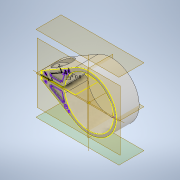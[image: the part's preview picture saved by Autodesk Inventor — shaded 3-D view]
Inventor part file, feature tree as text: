
AUTODESK INVENTOR PART (.ipt)
format: ipt  version: 2022 (Build 260153000, 153)  size: 346,112 bytes
history: native  units: mm
features: other x7, extrude x7, sketch x5, projected_geometry x4, fillet x2, mirror x1
ambient origin geometry x8: Origin, YZ Plane, XZ Plane, XY Plane, X Axis, Y Axis, Z Axis, Center Point
bodies: Body1 (feature_tree)
feature tree (26):
  other  "ソリッド1"
  extrude  "押し出し1"  Depth=31.9mm
  sketch  "スケッチ2"
  sketch  "スケッチ3"
  other  "作業平面1"
  other  "m6hole"
  mirror  "ミラー1"
  other  "HexagonSC"
  extrude  "押し出し2"  Depth=2.0mm
  extrude  "押し出し3"  TaperAngle=120.0deg  [1 undecoded]
  extrude  "押し出し4"  TaperAngle=150.0deg  [1 undecoded]
  sketch  "スケッチ7"
  sketch  "スケッチ8"
  other  "sidescetch"
  extrude  "押し出し5"  Depth=2.0mm
  extrude  "押し出し6"  Depth=2.0mm
  extrude  "押し出し7"  Depth=2.4mm
  fillet  "フィレット1"  Radius=0.8mm
  fillet  "フィレット2"  Radius=0.8mm
  other  "baseScetcj"
  projected_geometry  "投影ループ1"
  projected_geometry  "投影ループ2"
  projected_geometry  "投影ループ3"
  other  "作業平面2"
  sketch  "スケッチ6"
  projected_geometry  "投影ループ4"
note: 2 required parameter values undecoded (feature->parameter linkage not recoverable at this tier; creation-order binding heuristic only, values carry confidence <= 0.55)
